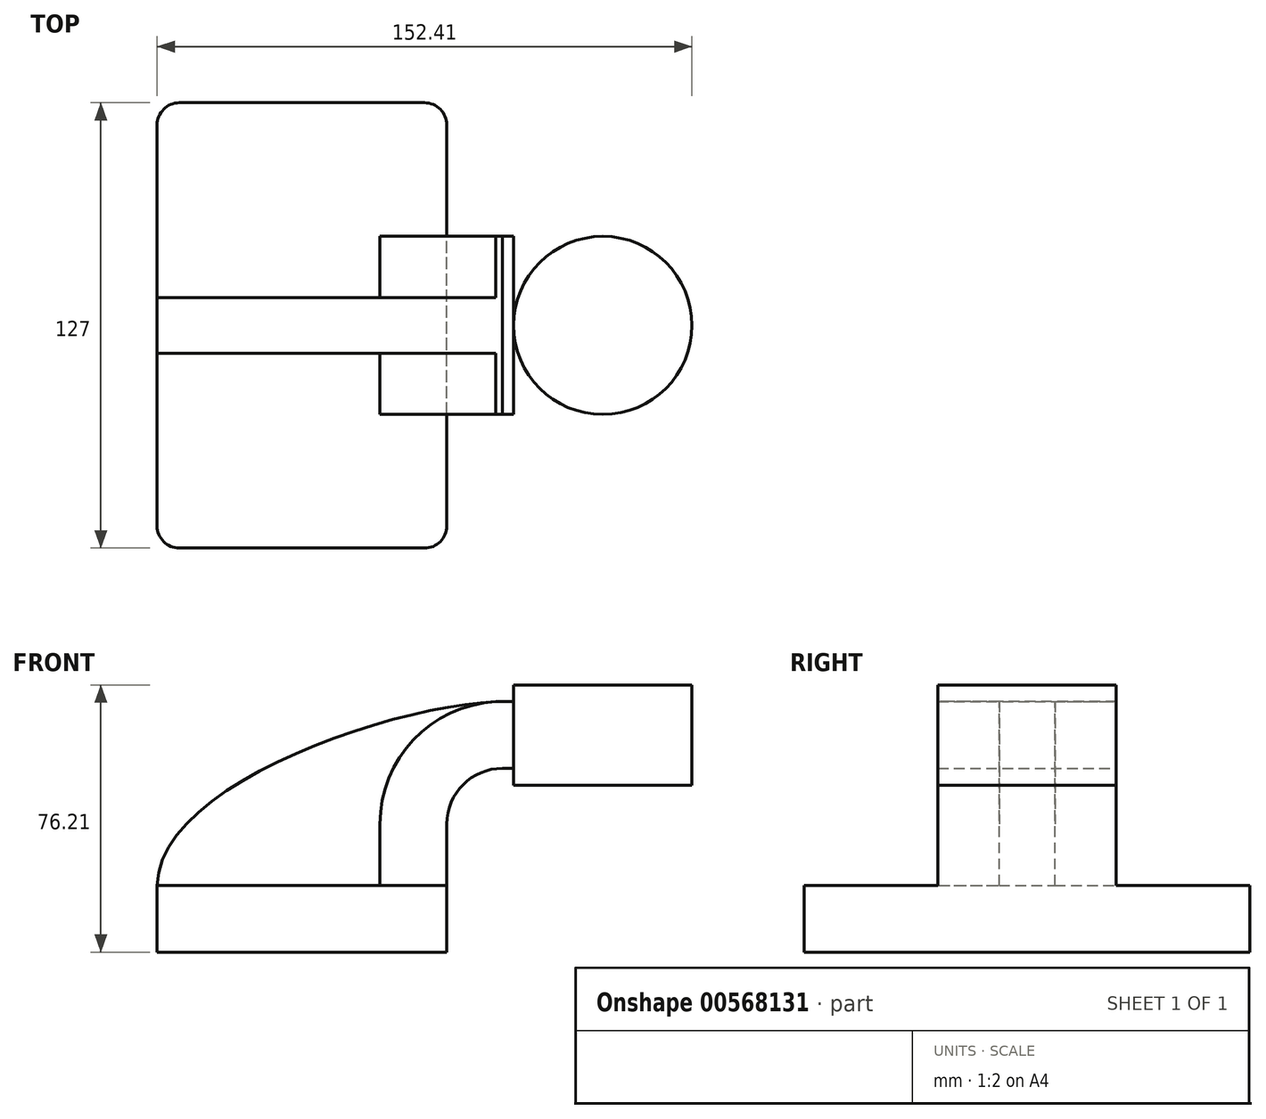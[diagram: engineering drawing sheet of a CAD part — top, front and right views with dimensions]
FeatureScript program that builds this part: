
annotation { "Feature Type Name" : "Feature", "Feature Type Description" : "" }
export const myFeature = defineFeature(function(context is Context, id is Id, definition is map)
    precondition{}
    {
        {
            var Q0;
            Q0=qCreatedBy(makeId("Front.planeOp"),FACE);
            var sketch = newSketch(context, id + "F0", { "sketchPlane" : qUnion([Q0])});
            skLineSegment(sketch, "E0.bottom", {"start": v(-41.28, 9.52) * mm, "end": v(41.27, 9.53) * mm});
            skLineSegment(sketch, "E0.top", {"start": v(-41.28, -9.53) * mm, "end": v(41.28, -9.53) * mm});
            skLineSegment(sketch, "E0.left", {"start": v(-41.28, 9.52) * mm, "end": v(-41.27, -9.53) * mm});
            skLineSegment(sketch, "E0.right", {"start": v(41.28, 9.53) * mm, "end": v(41.28, -9.52) * mm});
            skPoint(sketch, "E0.middle", {"position": v(0, 0) * mm});
            skLineSegment(sketch, "E1.bottom", {"start": v(60.32, 66.68) * mm, "end": v(111.12, 66.68) * mm});
            skLineSegment(sketch, "E1.top", {"start": v(60.32, 38.1) * mm, "end": v(111.12, 38.1) * mm});
            skLineSegment(sketch, "E1.left", {"start": v(60.32, 66.68) * mm, "end": v(60.32, 38.1) * mm});
            skLineSegment(sketch, "E1.right", {"start": v(111.12, 66.68) * mm, "end": v(111.12, 38.1) * mm});
            skPoint(sketch, "E1.middle", {"position": v(85.72, 52.39) * mm});
            skLineSegment(sketch, "E2", {"start": v(41.27, 9.53) * mm, "end": v(41.27, 27) * mm});
            skArc(sketch, "E3", {"start": v(41.27, 27) * mm, "mid": v(45.92, 38.23) * mm, "end": v(57.15, 42.88) * mm});
            skLineSegment(sketch, "E4", {"start": v(57.15, 42.88) * mm, "end": v(85.72, 42.88) * mm});
            skLineSegment(sketch, "E5.0", {"start": v(57.15, 61.93) * mm, "end": v(85.72, 61.93) * mm});
            skArc(sketch, "E5.1", {"start": v(22.23, 27) * mm, "mid": v(32.45, 51.7) * mm, "end": v(57.15, 61.93) * mm});
            skLineSegment(sketch, "E5.2", {"start": v(22.23, 9.53) * mm, "end": v(22.23, 27) * mm});
            skLineSegment(sketch, "E6", {"start": v(85.72, 38.1) * mm, "end": v(85.72, 66.68) * mm});
            skFitSpline(sketch, "E7", {"points": [v(-41.28, 9.52) * mm, v(57.15, 61.93) * mm], "startDerivative": vector(1.22, 87.49) * mm, "endDerivative": vector(89.22, 1.13) * mm});
            skSolve(sketch);
        }
        {
            var Q0;
            Q0=makeQuery(id+"F0.imprint","IMPRINT",FACE,{"disambiguationData":[TD([[makeQuery(id+"F0.imprint","IMPRINT",EDGE,{"derivedFrom":sQuery(id+"F0.wireOp",EDGE,"E0.top")}),1.0]])]});
            extrude(context, id + "F1", {"entities" : qUnion([Q0]), "endBound" : BoundingType.SYMMETRIC, "depth" : 127 * mm, "offsetDistance" : 25.4 * mm});
        }
        {
            var Q0;
            {var subQ1=sQuery(id+"F0.wireOp",EDGE,"E2");Q0=makeQuery(id+"F0.imprint","IMPRINT",FACE,{"disambiguationData":[TD([[makeQuery(id+"F0.imprint","IMPRINT",EDGE,{"derivedFrom":subQ1}),1.0]])]});}
            extrude(context, id + "F2", {"entities" : qUnion([Q0]), "operationType" : NewBodyOperationType.ADD, "endBound" : BoundingType.SYMMETRIC, "depth" : 50.8 * mm, "offsetDistance" : 25.4 * mm});
        }
        {
            var Q0;
            {var subQ3=sQuery(id+"F0.wireOp",EDGE,"E5.2");Q0=makeQuery(id+"F0.imprint","IMPRINT",FACE,{"disambiguationData":[TD([[makeQuery(id+"F0.imprint","IMPRINT",EDGE,{"derivedFrom":subQ3}),1.0]])]});}
            extrude(context, id + "F3", {"entities" : qUnion([Q0]), "operationType" : NewBodyOperationType.ADD, "endBound" : BoundingType.SYMMETRIC, "depth" : 15.88 * mm, "offsetDistance" : 25.4 * mm});
        }
        {
            var Q0;
            {var subQ4=sQuery(id+"F0.wireOp",EDGE,"E1.right");Q0=makeQuery(id+"F0.imprint","IMPRINT",FACE,{"disambiguationData":[TD([[makeQuery(id+"F0.imprint","IMPRINT",EDGE,{"derivedFrom":subQ4}),-1.0]])]});}
            var Q1;
            Q1=sQuery(id+"F0.wireOp",EDGE,"E6");
            revolve(context, id + "F4", {"operationType" : NewBodyOperationType.ADD, "entities" : qUnion([Q0]), "axis" : qUnion([Q1]), "revolveType" : RevolveType.FULL});
        }
        {
            var Q0;
            Q0=makeQuery(id+"F1.opExtrude","CAP_EDGE",EDGE,{"disambiguationData":[OSD([sQuery(id+"F0.wireOp",EDGE,"E0.left")])],"isStart":false});
            var Q1;
            Q1=makeQuery(id+"F1.opExtrude","CAP_EDGE",EDGE,{"disambiguationData":[OSD([sQuery(id+"F0.wireOp",EDGE,"E0.right")])],"isStart":false});
            var Q2;
            Q2=makeQuery(id+"F1.opExtrude","CAP_EDGE",EDGE,{"disambiguationData":[OSD([sQuery(id+"F0.wireOp",EDGE,"E0.right")])],"isStart":true});
            var Q3;
            Q3=makeQuery(id+"F1.opExtrude","CAP_EDGE",EDGE,{"disambiguationData":[OSD([sQuery(id+"F0.wireOp",EDGE,"E0.left")])],"isStart":true});
            fillet(context, id + "F5", {"entities" : qUnion([Q0, Q1, Q2, Q3]), "radius" : 6.35 * mm, "tangentPropagation" : true, "allowEdgeOverflow" : false});
        }
    });
